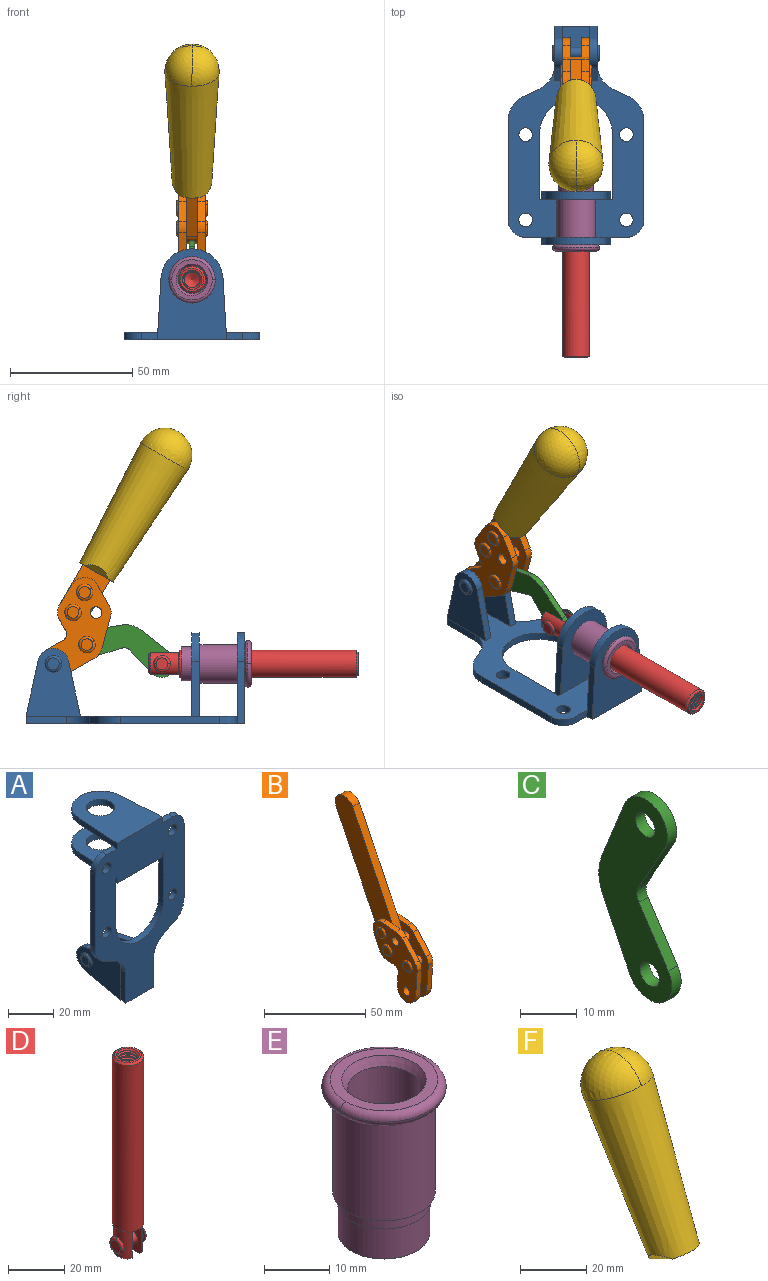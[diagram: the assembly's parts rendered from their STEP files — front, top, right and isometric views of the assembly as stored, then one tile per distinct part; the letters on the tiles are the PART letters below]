
ASSEMBLY  parts=6 mates=6
PART A: 55 faces, bbox 55.7x37.4x89.8 mm
  f0: torus R=2.41mm, axis (-1,0,0), area 15mm2, adj f11,f15,f25
  f1: torus R=2.41mm, axis (-1,0,0), area 15mm2, adj f10,f12,f22
  f2: cylinder r=2.78mm len=5.56mm, axis (0,-1,0), area 54.2mm2, adj f30,f54
  f3: cylinder r=14.99mm len=29.97mm, axis (0,-1,0), area 145.9mm2, adj f30,f49,f53,f54
  f4: cylinder r=2.78mm len=5.56mm, axis (0,-1,0), area 54.2mm2, adj f30,f54
  f5: cylinder r=2.78mm len=5.56mm, axis (0,-1,0), area 54.2mm2, adj f30,f54
  f6: cylinder r=2.78mm len=5.56mm, axis (0,-1,0), area 54.2mm2, adj f30,f54
  f7: cylinder r=6.35mm len=12.7mm, axis (0,0,1), area 123.6mm2, adj f27,f51
  f8: cylinder r=6.35mm len=12.7mm, axis (0,0,-1), area 124.7mm2, adj f21,f35
  f9: cylinder r=2.41mm len=11.18mm, axis (-1,0,0), area 169.4mm2, adj f16,f19
  f10: plane 4.83x4.83mm, normal (1,0,0), area 18.3mm2, adj f1,f12
  f11: plane 4.83x4.83mm, normal (-1,0,0), area 18.3mm2, adj f0,f15
  f12: torus R=2.41mm, axis (-1,0,0), area 15mm2, adj f1,f10,f22
  f13: cylinder r=6.35mm len=12.41mm, axis (1,0,0), area 53.4mm2, adj f18,f19,f22,f23
  f14: cylinder r=6.35mm len=12.41mm, axis (-1,0,0), area 53.4mm2, adj f16,f17,f24,f25
  f15: torus R=2.41mm, axis (-1,0,0), area 15mm2, adj f0,f11,f25
  f16: plane 27.86x22.35mm, normal (1,0,0), area 425.4mm2, adj f9,f14,f17,f24,f30
  f17: plane 22.86x4.97mm, normal (0,0.21,0.98), area 72.5mm2, adj f14,f16,f25,f30
  f18: plane 22.86x4.97mm, normal (0,0.21,0.98), area 72.5mm2, adj f13,f19,f22,f30
  f19: plane 27.86x22.35mm, normal (-1,0,0), area 425.4mm2, adj f9,f13,f18,f23,f30
  f20: cylinder r=12.7mm len=25.35mm, axis (0,0,-1), area 119.8mm2, adj f21,f34,f35,f36
  f21: plane 34.21x28.07mm, normal (0,0,-1), area 702.4mm2, adj f8,f20,f30,f34,f36
  f22: plane 27.96x22.45mm, normal (1,0,0), area 407.2mm2, adj f1,f12,f13,f18,f23,f30,f42,f43
  f23: plane 22.86x4.97mm, normal (0,0.21,-0.98), area 72.5mm2, adj f13,f19,f22,f44
  f24: plane 22.86x4.97mm, normal (0,0.21,-0.98), area 72.5mm2, adj f14,f16,f25,f44
  f25: plane 27.86x22.35mm, normal (-1,0,0), area 407.1mm2, adj f0,f14,f15,f17,f24,f30,f45,f46
  f26: plane 3.1x0.95mm, normal (0,0,-1), area 2.7mm2, adj f30,f49,f50,f54
  f27: plane 34.21x28.07mm, normal (0,0,1), area 702.4mm2, adj f7,f28,f30,f50,f52
  f28: cylinder r=12.7mm len=25.35mm, axis (0,0,1), area 118.8mm2, adj f27,f50,f51,f52
  f29: plane 3.1x0.95mm, normal (0,0,-1), area 2.7mm2, adj f30,f52,f53,f54
  f30: plane 86.54x55.63mm, normal (0,1,0), area 2362.9mm2, adj f2,f3,f4,f5,f6,f16,f17,f18
  f31: plane 40.56x3.1mm, normal (-1,0,0), area 125.7mm2, adj f30,f32,f48,f54
  f32: cylinder r=7.11mm len=7.11mm, axis (0,-1,0), area 34.6mm2, adj f30,f31,f33,f54
  f33: plane 6.67x3.1mm, normal (0,0,1), area 20.4mm2, adj f30,f32,f34,f54
  f34: plane 25.39x3.13mm, normal (-1,0.06,0), area 79.5mm2, adj f20,f21,f33,f35,f54
  f35: plane 37.31x28.45mm, normal (0,0,1), area 789.9mm2, adj f8,f20,f34,f36,f54
  f36: plane 25.39x3.13mm, normal (1,0.06,0), area 79.5mm2, adj f20,f21,f35,f37,f54
  f37: plane 6.67x3.1mm, normal (0,0,1), area 20.4mm2, adj f30,f36,f38,f54
  f38: cylinder r=7.11mm len=7.11mm, axis (0,-1,0), area 34.6mm2, adj f30,f37,f39,f54
  f39: plane 40.56x3.1mm, normal (1,0,0), area 125.7mm2, adj f30,f38,f40,f54
  f40: cylinder r=11.18mm len=10.16mm, axis (0,-1,0), area 39.5mm2, adj f30,f39,f41,f54
  f41: plane 6.09x3.1mm, normal (0.42,0,-0.91), area 20.8mm2, adj f30,f40,f42,f54
  f42: cylinder r=11.18mm len=9.41mm, axis (0,-1,0), area 37.2mm2, adj f22,f30,f41,f43,f54
  f43: plane 16.5x3.1mm, normal (1,0,0), area 51.1mm2, adj f22,f42,f44,f54
  f44: plane 17.37x3.1mm, normal (0,0,-1), area 53.8mm2, adj f23,f24,f30,f43,f45,f54
  f45: plane 16.5x3.1mm, normal (-1,0,0), area 51.1mm2, adj f25,f44,f46,f54
  f46: cylinder r=11.18mm len=9.41mm, axis (0,-1,0), area 37.2mm2, adj f25,f30,f45,f47,f54
  f47: plane 6.09x3.1mm, normal (-0.42,0,-0.91), area 20.8mm2, adj f30,f46,f48,f54
  f48: cylinder r=11.18mm len=10.16mm, axis (0,-1,0), area 39.5mm2, adj f30,f31,f47,f54
  f49: plane 26.54x3.1mm, normal (-1,0,0), area 82.3mm2, adj f3,f26,f30,f54
  f50: plane 25.39x3.1mm, normal (1,0.06,0), area 78.8mm2, adj f26,f27,f28,f51,f54
  f51: plane 37.31x28.45mm, normal (0,0,-1), area 789.9mm2, adj f7,f28,f50,f52,f54
  f52: plane 25.39x3.1mm, normal (-1,0.06,0), area 78.8mm2, adj f27,f28,f29,f51,f54
  f53: plane 26.54x3.1mm, normal (1,0,0), area 82.3mm2, adj f3,f29,f30,f54
  f54: plane 89.66x55.63mm, normal (0,-1,0), area 2678.5mm2, adj f2,f3,f4,f5,f6,f26,f29,f31
PART B: 59 faces, bbox 12.9x60.2x99.6 mm
  f0: torus R=2.39mm, axis (-1,0,0), area 14.9mm2, adj f20,f43,f51
  f1: torus R=2.39mm, axis (-1,0,0), area 14.9mm2, adj f19,f42,f51
  f2: torus R=2.39mm, axis (-1,0,0), area 14.9mm2, adj f18,f35,f51
  f3: torus R=2.39mm, axis (-1,0,0), area 14.9mm2, adj f14,f17,f23
  f4: torus R=2.39mm, axis (-1,0,0), area 14.9mm2, adj f13,f16,f23
  f5: torus R=2.39mm, axis (-1,0,0), area 14.9mm2, adj f12,f15,f23
  f6: cylinder r=2.39mm len=4.78mm, axis (1,0,0), area 46.5mm2, adj f48,f50,f51
  f7: cylinder r=2.39mm len=4.78mm, axis (1,0,0), area 46.5mm2, adj f50,f51
  f8: cylinder r=6.35mm len=12.68mm, axis (1,0,0), area 61.8mm2, adj f38,f39,f50,f51
  f9: cylinder r=2.39mm len=4.78mm, axis (-1,0,0), area 70.5mm2, adj f46,f50
  f10: cylinder r=2.39mm len=4.78mm, axis (-1,0,0), area 46.5mm2, adj f23,f45,f46
  f11: cylinder r=2.39mm len=4.78mm, axis (-1,0,0), area 46.5mm2, adj f23,f46
  f12: plane 4.78x4.78mm, normal (1,0,0), area 17.9mm2, adj f5,f15
  f13: plane 4.78x4.78mm, normal (1,0,0), area 17.9mm2, adj f4,f16
  f14: plane 4.78x4.78mm, normal (1,0,0), area 17.9mm2, adj f3,f17
  f15: torus R=2.39mm, axis (-1,0,0), area 14.9mm2, adj f5,f12,f23
  f16: torus R=2.39mm, axis (-1,0,0), area 14.9mm2, adj f4,f13,f23
  f17: torus R=2.39mm, axis (-1,0,0), area 14.9mm2, adj f3,f14,f23
  f18: plane 4.78x4.78mm, normal (-1,0,0), area 17.9mm2, adj f2,f35
  f19: plane 4.78x4.78mm, normal (-1,0,0), area 17.9mm2, adj f1,f42
  f20: plane 4.78x4.78mm, normal (-1,0,0), area 17.9mm2, adj f0,f43
  f21: plane 2.26x0.2mm, normal (1,0,0), area 0.2mm2, adj f31,f44
  f22: plane 2.26x0.2mm, normal (-1,0,0), area 0.2mm2, adj f41,f44
  f23: plane 39.37x30.77mm, normal (1,0,0), area 565.5mm2, adj f3,f4,f5,f10,f11,f15,f16,f17
  f24: cylinder r=6.1mm len=4.15mm, axis (-1,0,0), area 14.7mm2, adj f23,f25,f32,f46
  f25: plane 10.25x9.01mm, normal (0,-0.75,0.66), area 42.3mm2, adj f23,f24,f26,f46
  f26: cylinder r=6.35mm len=4.64mm, axis (-1,0,0), area 15.6mm2, adj f23,f25,f27,f46
  f27: plane 15.84x3.1mm, normal (0,-1,-0.07), area 49.2mm2, adj f23,f26,f28,f46
  f28: cylinder r=6.35mm len=12.68mm, axis (-1,0,0), area 61.8mm2, adj f23,f27,f29,f46
  f29: plane 8.11x3.1mm, normal (0,1,0.07), area 25.2mm2, adj f23,f28,f30,f46
  f30: cylinder r=3.05mm len=3.25mm, axis (-1,0,0), area 14.8mm2, adj f23,f29,f31,f46
  f31: plane 5.99x3.1mm, normal (0,0.07,-1), area 18.6mm2, adj f21,f23,f30,f44,f46
  f32: plane 9.5x3.1mm, normal (0,-0.07,1), area 29.5mm2, adj f23,f24,f33,f46,f47
  f33: cylinder r=6.1mm len=8.63mm, axis (-1,0,0), area 39.1mm2, adj f23,f32,f34,f47
  f34: plane 8.65x3.96mm, normal (0,0.91,-0.42), area 29.5mm2, adj f23,f33,f44,f47
  f35: torus R=2.39mm, axis (-1,0,0), area 14.9mm2, adj f2,f18,f51
  f36: plane 10.25x9.01mm, normal (0,-0.75,0.66), area 42.3mm2, adj f37,f49,f50,f51
  f37: cylinder r=6.35mm len=4.64mm, axis (1,0,0), area 15.6mm2, adj f36,f38,f50,f51
  f38: plane 15.84x3.1mm, normal (0,-1,-0.07), area 49.2mm2, adj f8,f37,f50,f51
  f39: plane 8.11x3.1mm, normal (0,1,0.07), area 25.2mm2, adj f8,f40,f50,f51
  f40: cylinder r=3.05mm len=3.25mm, axis (1,0,0), area 14.8mm2, adj f39,f41,f50,f51
  f41: plane 5.99x3.1mm, normal (0,0.07,-1), area 18.6mm2, adj f22,f40,f44,f50,f51
  f42: torus R=2.39mm, axis (-1,0,0), area 14.9mm2, adj f1,f19,f51
  f43: torus R=2.39mm, axis (-1,0,0), area 14.9mm2, adj f0,f20,f51
  f44: cylinder r=6.35mm len=12.12mm, axis (-1,0,0), area 128.9mm2, adj f21,f22,f23,f31,f34,f41,f46,f47
  f45: plane 2.65x1.35mm, normal (1,0,0), area 1mm2, adj f10,f55
  f46: plane 39.08x20.42mm, normal (-1,0,0), area 412.5mm2, adj f9,f10,f11,f24,f25,f26,f27,f28
  f47: plane 77.62x39.82mm, normal (1,0,0), area 850mm2, adj f32,f33,f34,f44,f53,f54,f55
  f48: plane 2.65x1.35mm, normal (-1,0,0), area 1mm2, adj f6,f55
  f49: cylinder r=6.1mm len=4.15mm, axis (1,0,0), area 14.7mm2, adj f36,f50,f51,f56
  f50: plane 39.08x20.42mm, normal (1,0,0), area 412.5mm2, adj f6,f7,f8,f9,f36,f37,f38,f39
  f51: plane 39.37x30.77mm, normal (-1,0,0), area 565.5mm2, adj f0,f1,f2,f6,f7,f8,f35,f36
  f52: plane 8.65x3.96mm, normal (0,0.91,-0.42), area 29.5mm2, adj f44,f51,f57,f58
  f53: plane 68.49x33.4mm, normal (0,0.9,-0.44), area 358.1mm2, adj f44,f47,f54,f58
  f54: cylinder r=6.35mm len=12.06mm, axis (1,0,0), area 93.7mm2, adj f47,f53,f55,f58
  f55: plane 68.49x33.4mm, normal (0,-0.9,0.44), area 358.1mm2, adj f44,f45,f46,f47,f48,f50,f54,f58
  f56: plane 9.5x3.1mm, normal (0,-0.07,1), area 29.5mm2, adj f49,f50,f51,f57,f58
  f57: cylinder r=6.1mm len=8.63mm, axis (1,0,0), area 39.1mm2, adj f51,f52,f56,f58
  f58: plane 77.62x39.82mm, normal (-1,0,0), area 850mm2, adj f44,f52,f53,f54,f55,f56,f57
PART C: 12 faces, bbox 2.3x18.2x42.8 mm
  f0: cylinder r=2.4mm len=4.8mm, axis (1,0,0), area 34.9mm2, adj f4,f11
  f1: cylinder r=10.41mm len=8.47mm, axis (1,0,0), area 20.2mm2, adj f4,f9,f10,f11
  f2: cylinder r=3.05mm len=3.16mm, axis (1,0,0), area 7.7mm2, adj f4,f6,f7,f11
  f3: cylinder r=2.4mm len=4.8mm, axis (1,0,0), area 34.9mm2, adj f4,f11
  f4: plane 42.81x18.23mm, normal (-1,0,0), area 414.1mm2, adj f0,f1,f2,f3,f5,f6,f7,f8
  f5: cylinder r=5.54mm len=10.67mm, axis (1,0,0), area 41.8mm2, adj f4,f6,f10,f11
  f6: plane 11.66x6.53mm, normal (0,-0.87,-0.49), area 30.9mm2, adj f2,f4,f5,f11
  f7: plane 11.17x7.33mm, normal (0,-0.84,0.55), area 30.9mm2, adj f2,f4,f8,f11
  f8: cylinder r=5.54mm len=10.51mm, axis (1,0,0), area 41.8mm2, adj f4,f7,f9,f11
  f9: plane 13.67x6.67mm, normal (0,0.9,-0.44), area 35.1mm2, adj f1,f4,f8,f11
  f10: plane 14.1x5.7mm, normal (0,0.93,0.37), area 35.1mm2, adj f1,f4,f5,f11
  f11: plane 42.81x18.23mm, normal (1,0,0), area 414.1mm2, adj f0,f1,f2,f3,f5,f6,f7,f8
PART D: 48 faces, bbox 12.6x11.1x86.1 mm
  f0: torus R=2.41mm, axis (-1,0,0), area 15mm2, adj f30,f32,f34
  f1: torus R=2.41mm, axis (-1,0,0), area 15mm2, adj f29,f31,f33
  f2: cylinder r=5.54mm len=72.39mm, axis (0,0,1), area 2518.5mm2, adj f3,f4,f42,f43
  f3: cone r=5.54mm half-angle=45deg, axis (0,0,1), area 7.6mm2, adj f2,f5,f41
  f4: cone r=5.54mm half-angle=45deg, axis (0,0,-1), area 34.9mm2, adj f2,f39
  f5: cylinder r=5.08mm len=11.48mm, axis (0,0,1), area 108.3mm2, adj f3,f7,f8,f41
  f6: cylinder r=2.41mm len=4.83mm, axis (-1,0,0), area 71.2mm2, adj f40,f41
  f7: cylinder r=2.41mm len=4.83mm, axis (-1,0,0), area 7.6mm2, adj f5,f34
  f8: cone r=5.08mm half-angle=45deg, axis (0,0,1), area 10.6mm2, adj f5,f37,f41
  f9: cone r=3.98mm half-angle=45deg, axis (0,0,1), area 17.6mm2, adj f27,f39,f45,f46,f47
  f10: cylinder r=2.41mm len=4.83mm, axis (-1,0,0), area 7.6mm2, adj f33,f38
  f11: cylinder r=3.2mm len=6.4mm, axis (0,0,1), area 78.4mm2, adj f12,f28,f44,f45,f47
  f12: cylinder r=3.2mm len=6.4mm, axis (0,0,1), area 10.5mm2, adj f11,f13,f45,f47
  f13: cylinder r=3.2mm len=6.4mm, axis (0,0,1), area 10.5mm2, adj f12,f14,f45,f47
  f14: cylinder r=3.2mm len=6.4mm, axis (0,0,1), area 10.5mm2, adj f13,f15,f45,f47
  f15: cylinder r=3.2mm len=6.4mm, axis (0,0,1), area 10.5mm2, adj f14,f16,f45,f47
  f16: cylinder r=3.2mm len=6.4mm, axis (0,0,1), area 10.5mm2, adj f15,f17,f45,f47
  f17: cylinder r=3.2mm len=6.4mm, axis (0,0,1), area 10.5mm2, adj f16,f18,f45,f47
  f18: cylinder r=3.2mm len=6.4mm, axis (0,0,1), area 10.5mm2, adj f17,f19,f45,f47
  f19: cylinder r=3.2mm len=6.4mm, axis (0,0,1), area 10.5mm2, adj f18,f20,f45,f47
  f20: cylinder r=3.2mm len=6.4mm, axis (0,0,1), area 10.5mm2, adj f19,f21,f45,f47
  f21: cylinder r=3.2mm len=6.4mm, axis (0,0,1), area 10.5mm2, adj f20,f22,f45,f47
  f22: cylinder r=3.2mm len=6.4mm, axis (0,0,1), area 10.5mm2, adj f21,f23,f45,f47
  f23: cylinder r=3.2mm len=6.4mm, axis (0,0,1), area 10.5mm2, adj f22,f24,f45,f47
  f24: cylinder r=3.2mm len=6.4mm, axis (0,0,1), area 10.5mm2, adj f23,f25,f45,f47
  f25: cylinder r=3.2mm len=6.4mm, axis (0,0,1), area 10.5mm2, adj f24,f26,f45,f47
  f26: cylinder r=3.2mm len=6.4mm, axis (0,0,1), area 10.5mm2, adj f25,f27,f45,f47
  f27: cylinder r=3.2mm len=6.4mm, axis (0,0,1), area 7.4mm2, adj f9,f26,f45,f47
  f28: cone r=3.2mm half-angle=60deg, axis (0,0,1), area 37.2mm2, adj f11
  f29: plane 4.83x4.83mm, normal (-1,0,0), area 18.3mm2, adj f1,f31
  f30: plane 4.83x4.83mm, normal (1,0,0), area 18.3mm2, adj f0,f32
  f31: torus R=2.41mm, axis (-1,0,0), area 15mm2, adj f1,f29,f33
  f32: torus R=2.41mm, axis (-1,0,0), area 15mm2, adj f0,f30,f34
  f33: plane 6.83x6.83mm, normal (1,0,0), area 18.3mm2, adj f1,f10,f31
  f34: plane 6.83x6.83mm, normal (-1,0,0), area 18.3mm2, adj f0,f7,f32
  f35: cone r=5.08mm half-angle=45deg, axis (0,0,1), area 10.6mm2, adj f36,f38,f40
  f36: plane 7.25x1.97mm, normal (0,0,-1), area 10mm2, adj f35,f40
  f37: plane 7.25x1.97mm, normal (0,0,-1), area 10mm2, adj f8,f41
  f38: cylinder r=5.08mm len=11.48mm, axis (0,0,1), area 108.3mm2, adj f10,f35,f40,f42
  f39: plane 9.55x9.55mm, normal (0,0,1), area 22mm2, adj f4,f9
  f40: plane 12.76x10.09mm, normal (1,0,0), area 95.7mm2, adj f6,f35,f36,f38,f42,f43
  f41: plane 12.76x10.09mm, normal (-1,0,0), area 95.7mm2, adj f3,f5,f6,f8,f37,f43
  f42: cone r=5.54mm half-angle=45deg, axis (0,0,1), area 7.6mm2, adj f2,f38,f40
  f43: plane 11.07x4.7mm, normal (0,0,-1), area 50.4mm2, adj f2,f40,f41
  f44: plane 0.89x0.62mm, normal (-1,0,0), area 0.3mm2, adj f11,f45,f46,f47
  f45: bspline ~24.8x7.63mm, area 266.6mm2, adj f9,f11,f12,f13,f14,f15,f16,f17
  f46: bspline ~24.87x7.63mm, area 73.6mm2, adj f9,f44,f45,f47
  f47: bspline ~24.98x7.63mm, area 272.5mm2, adj f9,f11,f12,f13,f14,f15,f16,f17
PART E: 15 faces, bbox 20.6x20.6x28.7 mm
  f0: torus R=8.26mm, axis (0,0,1), area 56.8mm2, adj f1,f10,f12
  f1: torus R=8.26mm, axis (0,0,1), area 56.8mm2, adj f0,f6,f13
  f2: cylinder r=5.59mm len=25.91mm, axis (0,0,1), area 909.6mm2, adj f3,f4
  f3: cone r=6.86mm half-angle=45deg, axis (0,0,-1), area 70.2mm2, adj f2,f14
  f4: cone r=6.47mm half-angle=30deg, axis (0,0,1), area 66.7mm2, adj f2,f13
  f5: cylinder r=7.04mm len=14.07mm, axis (0,0,1), area 252.6mm2, adj f11,f14
  f6: torus R=8.26mm, axis (0,0,1), area 56.8mm2, adj f1,f12,f13
  f7: cylinder r=7.16mm len=14.33mm, axis (0,0,1), area 91.5mm2, adj f9,f11
  f8: cylinder r=7.86mm len=18.42mm, axis (0,0,1), area 909.6mm2, adj f9,f10
  f9: plane 15.72x15.72mm, normal (0,0,-1), area 33mm2, adj f7,f8
  f10: plane 16.51x16.51mm, normal (0,0,-1), area 19.9mm2, adj f0,f8,f12
  f11: plane 14.33x14.33mm, normal (0,0,-1), area 5.7mm2, adj f5,f7
  f12: torus R=8.26mm, axis (0,0,1), area 56.8mm2, adj f0,f6,f10
  f13: plane 16.51x16.51mm, normal (0,0,1), area 82.7mm2, adj f1,f4,f6
  f14: plane 14.07x14.07mm, normal (0,0,-1), area 7.8mm2, adj f3,f5
PART F: 11 faces, bbox 22.3x42.6x64.5 mm
  f0: sphere r=11.13mm, area 411.4mm2, adj f1,f8
  f1: cone r=11.11mm half-angle=3.3deg, axis (0,0.44,0.9), area 3251.8mm2, adj f0,f7,f8,f9,f10
  f2: cylinder r=6.16mm len=11.7mm, axis (1,0,0), area 89.5mm2, adj f3,f4,f5,f6
  f3: plane 60.23x36.75mm, normal (-1,0,0), area 763.6mm2, adj f2,f4,f6,f10
  f4: plane 51.37x25.05mm, normal (0,0.9,-0.44), area 264.2mm2, adj f2,f3,f5,f10
  f5: plane 60.23x36.75mm, normal (1,0,0), area 763.6mm2, adj f2,f4,f6,f10
  f6: plane 51.37x25.05mm, normal (0,-0.9,0.44), area 264.2mm2, adj f2,f3,f5,f10
  f7: plane 9.95x5.95mm, normal (0.71,-0.31,-0.64), area 25.8mm2, adj f1,f10
  f8: sphere r=11.13mm, area 411.4mm2, adj f0,f1
  f9: plane 9.95x5.95mm, normal (-0.71,-0.31,-0.64), area 25.8mm2, adj f1,f10
  f10: plane 14.27x11.38mm, normal (0,-0.44,-0.9), area 106.7mm2, adj f1,f3,f4,f5,f6,f7,f9
PLACE A rot(axis=(1,0,0),90deg) t=(0,9.14,0)mm fixed
PLACE B rot(axis=(1,0,0),56.3deg) t=(0,0.88,21.94)mm
PLACE C rot(axis=(0,-0.63,-0.78),180deg) t=(0,17.59,5.13)mm
PLACE D rot(axis=(1,0,0),90deg) t=(0,12.16,0)mm
PLACE E rot(axis=(1,0,0),90deg) t=(0,9.14,0)mm
PLACE F rot(axis=(1,0,0),56.3deg) t=(0,0.88,21.94)mm
MATE slider D.f2 <-> A.f7  axis (0,-1,0) through (0,-46.62,24.61)mm
MATE revolute A.f0 <-> B.f7  axis (-1,0,0) through (0,41.23,24.61)mm
MATE revolute C.f5 <-> B.f4  axis (-1,0,0) through (0,27.44,32.48)mm
MATE fastened A.f7 <-> E.f0  axis (0,1,0) through (0,-37.25,24.61)mm
MATE revolute C.f3 <-> D.f6  axis (-1,0,0) through (0,-3.32,24.61)mm
MATE fastened F.f2 <-> B.f54  axis (1,0,0) through (0,-5.27,111.44)mm
